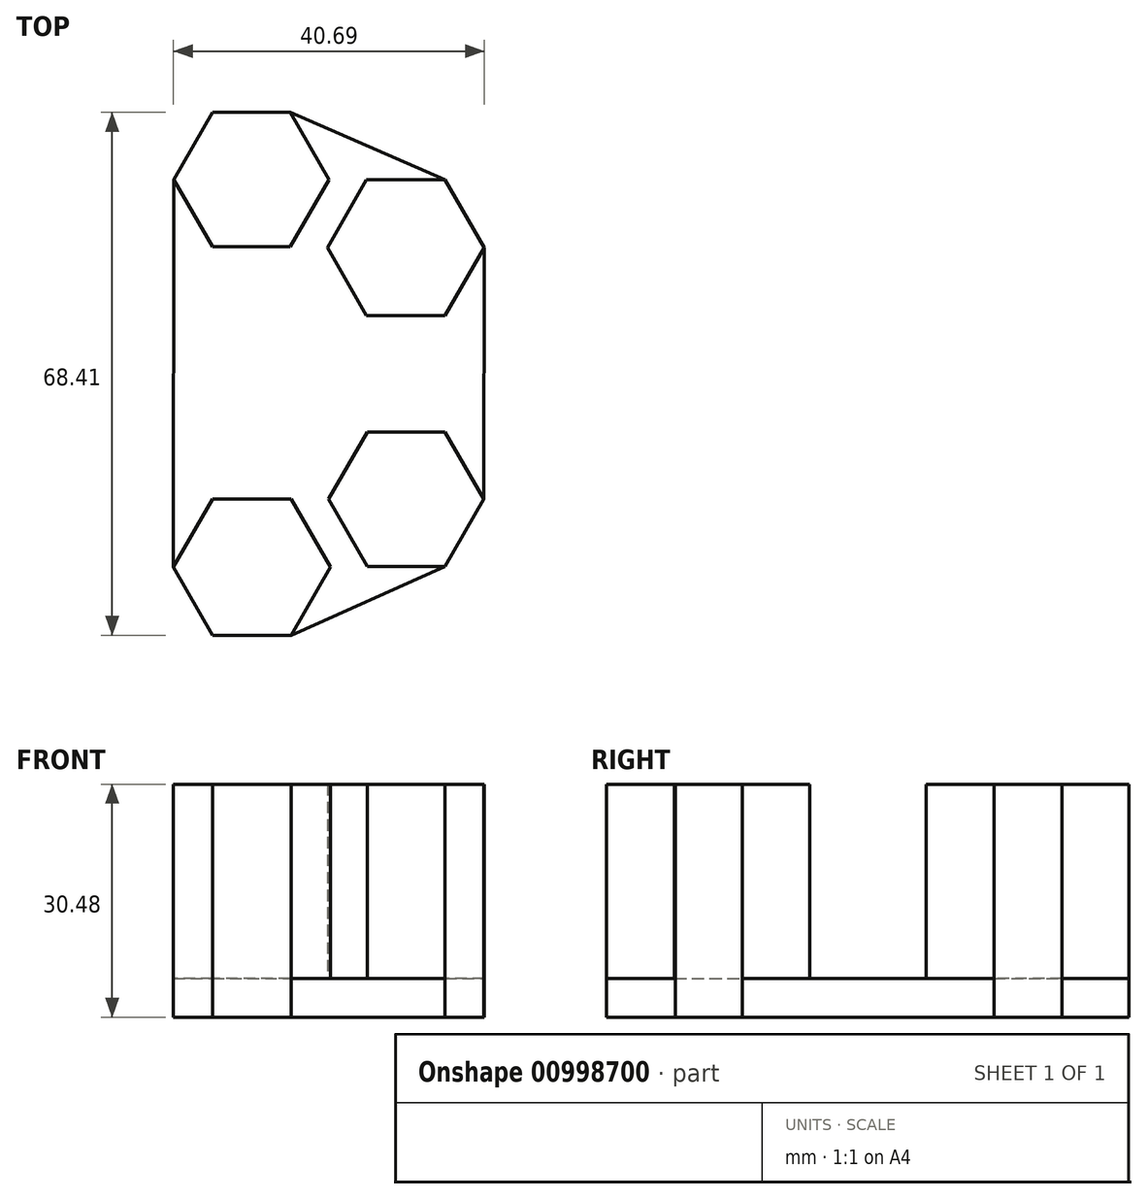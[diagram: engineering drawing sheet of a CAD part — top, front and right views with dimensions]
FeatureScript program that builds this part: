
annotation { "Feature Type Name" : "Feature", "Feature Type Description" : "" }
export const myFeature = defineFeature(function(context is Context, id is Id, definition is map)
    precondition{}
    {
        {
            var Q0;
            Q0=qCreatedBy(makeId("Top.planeOp"),FACE);
            var sketch = newSketch(context, id + "F0", { "sketchPlane" : qUnion([Q0])});
            skLineSegment(sketch, "E0", {"start": v(-46.58, 14.15) * mm, "end": v(-51.66, 5.35) * mm});
            skLineSegment(sketch, "E1", {"start": v(-51.66, 5.35) * mm, "end": v(-46.58, -3.45) * mm});
            skLineSegment(sketch, "E2", {"start": v(-46.58, -3.45) * mm, "end": v(-36.42, -3.45) * mm});
            skLineSegment(sketch, "E3", {"start": v(-36.42, -3.45) * mm, "end": v(-31.34, 5.35) * mm});
            skLineSegment(sketch, "E4", {"start": v(-31.34, 5.35) * mm, "end": v(-36.42, 14.15) * mm});
            skLineSegment(sketch, "E5", {"start": v(-36.42, 14.15) * mm, "end": v(-46.58, 14.15) * mm});
            skLineSegment(sketch, "E6", {"start": v(-26.42, 5.35) * mm, "end": v(-31.56, -3.54) * mm});
            skLineSegment(sketch, "E7", {"start": v(-31.56, -3.54) * mm, "end": v(-26.42, -12.44) * mm});
            skLineSegment(sketch, "E8", {"start": v(-26.42, -12.44) * mm, "end": v(-16.15, -12.44) * mm});
            skLineSegment(sketch, "E9", {"start": v(-16.15, -12.44) * mm, "end": v(-11.02, -3.54) * mm});
            skLineSegment(sketch, "E10", {"start": v(-11.02, -3.54) * mm, "end": v(-16.15, 5.35) * mm});
            skLineSegment(sketch, "E11", {"start": v(-16.15, 5.35) * mm, "end": v(-26.42, 5.35) * mm});
            skLineSegment(sketch, "E12", {"start": v(-46.58, -36.47) * mm, "end": v(-51.71, -45.37) * mm});
            skLineSegment(sketch, "E13", {"start": v(-51.71, -45.37) * mm, "end": v(-46.58, -54.26) * mm});
            skLineSegment(sketch, "E14", {"start": v(-46.58, -54.26) * mm, "end": v(-36.3, -54.26) * mm});
            skLineSegment(sketch, "E15", {"start": v(-36.3, -54.26) * mm, "end": v(-31.17, -45.37) * mm});
            skLineSegment(sketch, "E16", {"start": v(-31.17, -45.37) * mm, "end": v(-36.3, -36.47) * mm});
            skLineSegment(sketch, "E17", {"start": v(-36.3, -36.47) * mm, "end": v(-46.58, -36.47) * mm});
            skLineSegment(sketch, "E18", {"start": v(-26.31, -27.68) * mm, "end": v(-31.4, -36.47) * mm});
            skLineSegment(sketch, "E19", {"start": v(-31.4, -36.47) * mm, "end": v(-26.31, -45.27) * mm});
            skLineSegment(sketch, "E20", {"start": v(-26.31, -45.27) * mm, "end": v(-16.15, -45.27) * mm});
            skLineSegment(sketch, "E21", {"start": v(-16.15, -45.27) * mm, "end": v(-11.07, -36.47) * mm});
            skLineSegment(sketch, "E22", {"start": v(-11.07, -36.47) * mm, "end": v(-16.15, -27.68) * mm});
            skLineSegment(sketch, "E23", {"start": v(-16.15, -27.68) * mm, "end": v(-26.31, -27.68) * mm});
            skLineSegment(sketch, "E24", {"start": v(-16.15, 5.35) * mm, "end": v(-36.42, 14.15) * mm});
            skLineSegment(sketch, "E25", {"start": v(-51.66, 5.35) * mm, "end": v(-51.71, -45.37) * mm});
            skLineSegment(sketch, "E26", {"start": v(-36.3, -54.26) * mm, "end": v(-16.15, -45.27) * mm});
            skLineSegment(sketch, "E27", {"start": v(-11.07, -36.47) * mm, "end": v(-11.02, -3.54) * mm});
            skLineSegment(sketch, "E28", {"start": v(-16.15, 28.53) * mm, "end": v(-16.15, 13.3) * mm, "construction": true});
            skLineSegment(sketch, "E29", {"start": v(-46.58, 32.55) * mm, "end": v(-46.58, 18.49) * mm, "construction": true});
            skSolve(sketch);
        }
        {
            var Q0;
            Q0=makeQuery(id+"F0.imprint","IMPRINT",FACE,{"disambiguationData":[TD([[makeQuery(id+"F0.imprint","IMPRINT",EDGE,{"derivedFrom":sQuery(id+"F0.wireOp",EDGE,"E0")}),1.0]])]});
            var Q1;
            Q1=makeQuery(id+"F0.imprint","IMPRINT",FACE,{"disambiguationData":[TD([[makeQuery(id+"F0.imprint","IMPRINT",EDGE,{"derivedFrom":sQuery(id+"F0.wireOp",EDGE,"E6")}),1.0]])]});
            var Q2;
            Q2=makeQuery(id+"F0.imprint","IMPRINT",FACE,{"disambiguationData":[TD([[makeQuery(id+"F0.imprint","IMPRINT",EDGE,{"derivedFrom":sQuery(id+"F0.wireOp",EDGE,"E18")}),1.0]])]});
            var Q3;
            Q3=makeQuery(id+"F0.imprint","IMPRINT",FACE,{"disambiguationData":[TD([[makeQuery(id+"F0.imprint","IMPRINT",EDGE,{"derivedFrom":sQuery(id+"F0.wireOp",EDGE,"E12")}),1.0]])]});
            var Q4;
            Q4=makeQuery(id+"F0.imprint","IMPRINT",FACE,{"disambiguationData":[TD([[makeQuery(id+"F0.imprint","IMPRINT",EDGE,{"derivedFrom":sQuery(id+"F0.wireOp",EDGE,"E1")}),-1.0]])]});
            extrude(context, id + "F1", {"entities" : qUnion([Q0, Q1, Q2, Q3, Q4]), "depth" : 5.08 * mm, "offsetDistance" : 25.4 * mm});
        }
        {
            var Q0;
            Q0=makeQuery(id+"F0.imprint","IMPRINT",FACE,{"disambiguationData":[TD([[makeQuery(id+"F0.imprint","IMPRINT",EDGE,{"derivedFrom":sQuery(id+"F0.wireOp",EDGE,"E0")}),1.0]])]});
            var Q1;
            Q1=makeQuery(id+"F0.imprint","IMPRINT",FACE,{"disambiguationData":[TD([[makeQuery(id+"F0.imprint","IMPRINT",EDGE,{"derivedFrom":sQuery(id+"F0.wireOp",EDGE,"E6")}),1.0]])]});
            var Q2;
            Q2=makeQuery(id+"F0.imprint","IMPRINT",FACE,{"disambiguationData":[TD([[makeQuery(id+"F0.imprint","IMPRINT",EDGE,{"derivedFrom":sQuery(id+"F0.wireOp",EDGE,"E18")}),1.0]])]});
            var Q3;
            Q3=makeQuery(id+"F0.imprint","IMPRINT",FACE,{"disambiguationData":[TD([[makeQuery(id+"F0.imprint","IMPRINT",EDGE,{"derivedFrom":sQuery(id+"F0.wireOp",EDGE,"E12")}),1.0]])]});
            extrude(context, id + "F2", {"entities" : qUnion([Q0, Q1, Q2, Q3]), "operationType" : NewBodyOperationType.ADD, "depth" : 30.48 * mm, "offsetDistance" : 25.4 * mm});
        }
    });
